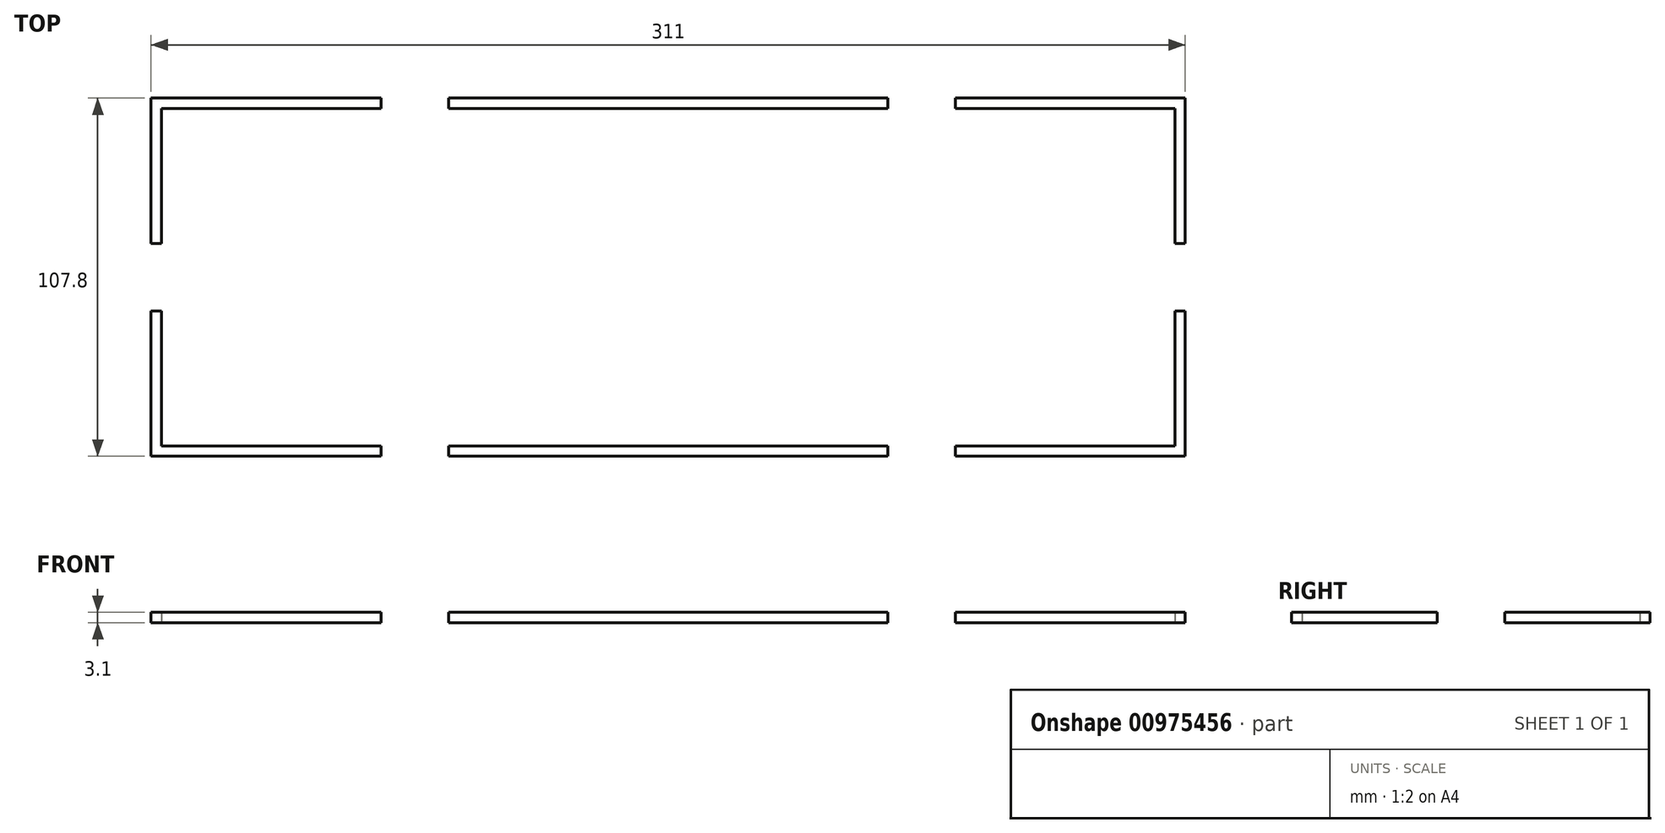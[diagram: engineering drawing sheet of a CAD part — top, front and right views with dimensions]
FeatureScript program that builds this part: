
annotation { "Feature Type Name" : "Feature", "Feature Type Description" : "" }
export const myFeature = defineFeature(function(context is Context, id is Id, definition is map)
    precondition{}
    {
        {
            var Q0;
            Q0=qCreatedBy(makeId("Top.planeOp"),FACE);
            var sketch = newSketch(context, id + "F0", { "sketchPlane" : qUnion([Q0])});
            skLineSegment(sketch, "E0.bottom", {"start": v(0, 0) * mm, "end": v(304.8, 0) * mm});
            skLineSegment(sketch, "E0.top", {"start": v(0, 101.6) * mm, "end": v(304.8, 101.6) * mm});
            skLineSegment(sketch, "E0.left", {"start": v(0, 0) * mm, "end": v(0, 101.6) * mm});
            skLineSegment(sketch, "E0.right", {"start": v(304.8, 0) * mm, "end": v(304.8, 101.6) * mm});
            skLineSegment(sketch, "E1.top", {"start": v(0, 104.7) * mm, "end": v(304.8, 104.7) * mm});
            skLineSegment(sketch, "E1.left", {"start": v(0, 101.6) * mm, "end": v(0, 104.7) * mm});
            skLineSegment(sketch, "E1.right", {"start": v(304.8, 101.6) * mm, "end": v(304.8, 104.7) * mm});
            skLineSegment(sketch, "E2.bottom", {"start": v(66.04, 104.7) * mm, "end": v(86.36, 104.7) * mm});
            skLineSegment(sketch, "E2.top", {"start": v(66.04, 101.6) * mm, "end": v(86.36, 101.6) * mm});
            skLineSegment(sketch, "E2.left", {"start": v(66.04, 104.7) * mm, "end": v(66.04, 101.6) * mm});
            skLineSegment(sketch, "E2.right", {"start": v(86.36, 104.7) * mm, "end": v(86.36, 101.6) * mm});
            skLineSegment(sketch, "E3", {"start": v(152.4, 101.6) * mm, "end": v(152.4, 0) * mm, "construction": true});
            skLineSegment(sketch, "E4", {"start": v(76.2, 104.7) * mm, "end": v(76.2, 0) * mm, "construction": true});
            skLineSegment(sketch, "E5", {"start": v(0, 50.8) * mm, "end": v(304.8, 50.8) * mm, "construction": true});
            skLineSegment(sketch, "E6.MirrorCS", {"start": v(66.04, -3.1) * mm, "end": v(66.04, 0) * mm});
            skLineSegment(sketch, "E7.MirrorCS", {"start": v(0, -3.1) * mm, "end": v(304.8, -3.1) * mm});
            skLineSegment(sketch, "E8.MirrorCS", {"start": v(86.36, -3.1) * mm, "end": v(86.36, 0) * mm});
            skLineSegment(sketch, "E9.MirrorCS", {"start": v(304.8, 0) * mm, "end": v(304.8, -3.1) * mm});
            skLineSegment(sketch, "E10.MirrorCS", {"start": v(0, 0) * mm, "end": v(0, -3.1) * mm});
            skLineSegment(sketch, "E11.bottom", {"start": v(0, 104.7) * mm, "end": v(-3.1, 104.7) * mm});
            skLineSegment(sketch, "E11.top", {"start": v(0, -3.1) * mm, "end": v(-3.1, -3.1) * mm});
            skLineSegment(sketch, "E11.left", {"start": v(0, 104.7) * mm, "end": v(0, -3.1) * mm});
            skLineSegment(sketch, "E11.right", {"start": v(-3.1, 104.7) * mm, "end": v(-3.1, -3.1) * mm});
            skLineSegment(sketch, "E12.bottom", {"start": v(-3.1, 60.96) * mm, "end": v(0, 60.96) * mm});
            skLineSegment(sketch, "E12.top", {"start": v(-3.1, 40.64) * mm, "end": v(0, 40.64) * mm});
            skLineSegment(sketch, "E12.left", {"start": v(-3.1, 60.96) * mm, "end": v(-3.1, 40.64) * mm});
            skLineSegment(sketch, "E12.right", {"start": v(0, 60.96) * mm, "end": v(0, 40.64) * mm});
            skLineSegment(sketch, "E13.MirrorCS", {"start": v(238.76, 104.7) * mm, "end": v(238.76, 101.6) * mm});
            skLineSegment(sketch, "E14.MirrorCS", {"start": v(218.44, 104.7) * mm, "end": v(218.44, 101.6) * mm});
            skLineSegment(sketch, "E15.MirrorCS", {"start": v(238.76, -3.1) * mm, "end": v(238.76, 0) * mm});
            skLineSegment(sketch, "E16.MirrorCS", {"start": v(218.44, -3.1) * mm, "end": v(218.44, 0) * mm});
            skLineSegment(sketch, "E17.MirrorCS", {"start": v(307.9, 104.7) * mm, "end": v(307.9, -3.1) * mm});
            skLineSegment(sketch, "E18.MirrorCS", {"start": v(304.8, -3.1) * mm, "end": v(307.9, -3.1) * mm});
            skLineSegment(sketch, "E19.MirrorCS", {"start": v(304.8, 104.7) * mm, "end": v(307.9, 104.7) * mm});
            skLineSegment(sketch, "E20.MirrorCS", {"start": v(307.9, 60.96) * mm, "end": v(304.8, 60.96) * mm});
            skLineSegment(sketch, "E21.MirrorCS", {"start": v(307.9, 40.64) * mm, "end": v(304.8, 40.64) * mm});
            skSolve(sketch);
        }
        {
            var Q0;
            {var subQ0=sQuery(id+"F0.wireOp",EDGE,"E2.top");Q0=makeQuery(id+"F0.imprint","IMPRINT",FACE,{"disambiguationData":[TD([[makeQuery(id+"F0.imprint","IMPRINT",EDGE,{"derivedFrom":subQ0}),-1.0]])]});}
            var Q1;
            {var subQ1=sQuery(id+"F0.wireOp",EDGE,"E11.bottom");Q1=makeQuery(id+"F0.imprint","IMPRINT",FACE,{"disambiguationData":[TD([[makeQuery(id+"F0.imprint","IMPRINT",EDGE,{"derivedFrom":subQ1}),1.0]])]});}
            var Q2;
            {var subQ3=sQuery(id+"F0.wireOp",EDGE,"E2.left");Q2=makeQuery(id+"F0.imprint","IMPRINT",FACE,{"disambiguationData":[TD([[makeQuery(id+"F0.imprint","IMPRINT",EDGE,{"derivedFrom":subQ3}),-1.0]])]});}
            var Q3;
            {var subQ1=sQuery(id+"F0.wireOp",EDGE,"E11.top");Q3=makeQuery(id+"F0.imprint","IMPRINT",FACE,{"disambiguationData":[TD([[makeQuery(id+"F0.imprint","IMPRINT",EDGE,{"derivedFrom":subQ1}),-1.0]])]});}
            var Q4;
            {var subQ3=sQuery(id+"F0.wireOp",EDGE,"E6.MirrorCS");Q4=makeQuery(id+"F0.imprint","IMPRINT",FACE,{"disambiguationData":[TD([[makeQuery(id+"F0.imprint","IMPRINT",EDGE,{"derivedFrom":subQ3}),1.0]])]});}
            var Q5;
            {var subQ0=sQuery(id+"F0.wireOp",EDGE,"E8.MirrorCS");Q5=makeQuery(id+"F0.imprint","IMPRINT",FACE,{"disambiguationData":[TD([[makeQuery(id+"F0.imprint","IMPRINT",EDGE,{"derivedFrom":subQ0}),-1.0]])]});}
            var Q6;
            {var subQ0=sQuery(id+"F0.wireOp",EDGE,"E2.right");Q6=makeQuery(id+"F0.imprint","IMPRINT",FACE,{"disambiguationData":[TD([[makeQuery(id+"F0.imprint","IMPRINT",EDGE,{"derivedFrom":subQ0}),1.0]])]});}
            var Q7;
            {var subQ0=sQuery(id+"F0.wireOp",EDGE,"E9.MirrorCS");Q7=makeQuery(id+"F0.imprint","IMPRINT",FACE,{"disambiguationData":[TD([[makeQuery(id+"F0.imprint","IMPRINT",EDGE,{"derivedFrom":subQ0}),-1.0]])]});}
            var Q8;
            {var subQ3=sQuery(id+"F0.wireOp",EDGE,"E9.MirrorCS");Q8=makeQuery(id+"F0.imprint","IMPRINT",FACE,{"disambiguationData":[TD([[makeQuery(id+"F0.imprint","IMPRINT",EDGE,{"derivedFrom":subQ3}),1.0]])]});}
            var Q9;
            {var subQ1=sQuery(id+"F0.wireOp",EDGE,"E1.right");Q9=makeQuery(id+"F0.imprint","IMPRINT",FACE,{"disambiguationData":[TD([[makeQuery(id+"F0.imprint","IMPRINT",EDGE,{"derivedFrom":subQ1}),-1.0]])]});}
            var Q10;
            {var subQ0=sQuery(id+"F0.wireOp",EDGE,"E1.right");Q10=makeQuery(id+"F0.imprint","IMPRINT",FACE,{"disambiguationData":[TD([[makeQuery(id+"F0.imprint","IMPRINT",EDGE,{"derivedFrom":subQ0}),1.0]])]});}
            extrude(context, id + "F1", {"entities" : qUnion([Q0, Q1, Q2, Q3, Q4, Q5, Q6, Q7, Q8, Q9, Q10]), "depth" : 3.1 * mm, "offsetDistance" : 25.4 * mm});
        }
    });
